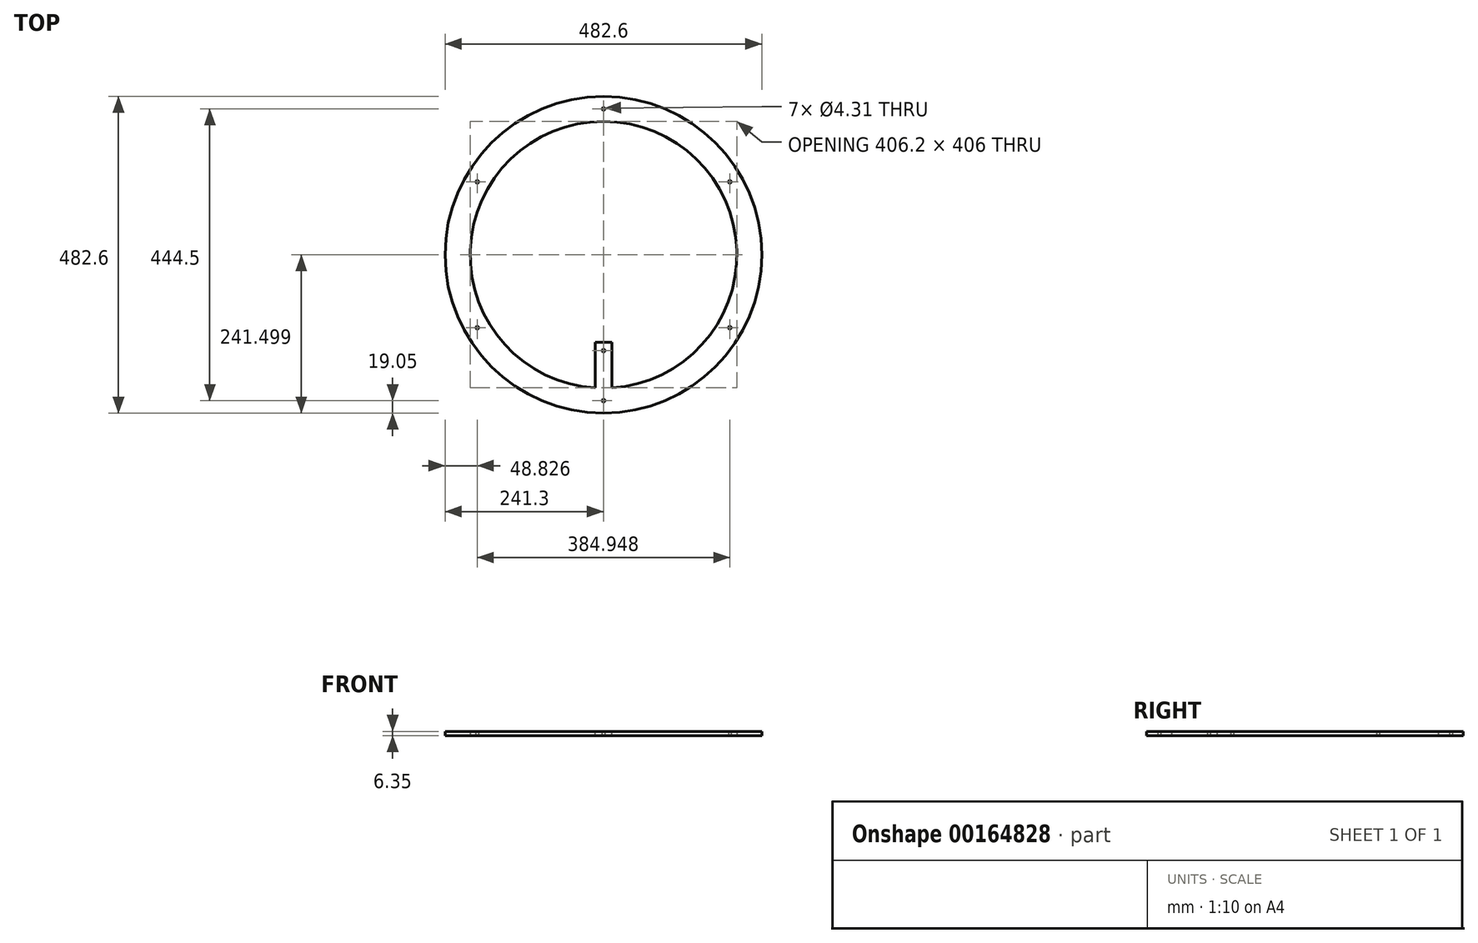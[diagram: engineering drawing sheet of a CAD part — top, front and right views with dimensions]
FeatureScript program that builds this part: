
annotation { "Feature Type Name" : "Feature", "Feature Type Description" : "" }
export const myFeature = defineFeature(function(context is Context, id is Id, definition is map)
    precondition{}
    {
        {
            var Q0;
            Q0=qCreatedBy(makeId("Top.planeOp"),FACE);
            var sketch = newSketch(context, id + "F0", { "sketchPlane" : qUnion([Q0])});
            skCircle(sketch, "E0", {"center": v(0, 0) * mm, "radius": 241.3 * mm});
            skCircle(sketch, "E1", {"center": v(0, 0) * mm, "radius": 203.2 * mm});
            skCircle(sketch, "E2.cCircle", {"center": v(0, 0) * mm, "radius": 192.47 * mm, "construction": true});
            skLineSegment(sketch, "E2.0", {"start": v(192.47, 111.13) * mm, "end": v(192.47, -111.12) * mm, "construction": true});
            skLineSegment(sketch, "E2.1", {"start": v(192.47, -111.12) * mm, "end": v(0, -222.25) * mm, "construction": true});
            skLineSegment(sketch, "E2.2", {"start": v(0, -222.25) * mm, "end": v(-192.47, -111.12) * mm, "construction": true});
            skLineSegment(sketch, "E2.3", {"start": v(-192.47, -111.13) * mm, "end": v(-192.47, 111.12) * mm, "construction": true});
            skLineSegment(sketch, "E2.4", {"start": v(-192.47, 111.12) * mm, "end": v(0, 222.25) * mm, "construction": true});
            skLineSegment(sketch, "E2.5", {"start": v(0, 222.25) * mm, "end": v(192.47, 111.12) * mm, "construction": true});
            skCircle(sketch, "E3", {"center": v(192.47, -111.12) * mm, "radius": 19.05 * mm, "construction": true});
            skCircle(sketch, "E4", {"center": v(192.47, -111.12) * mm, "radius": 2.15 * mm});
            skCircle(sketch, "E5", {"center": v(0, -222.25) * mm, "radius": 2.15 * mm});
            skCircle(sketch, "E6", {"center": v(-192.47, -111.13) * mm, "radius": 2.15 * mm});
            skCircle(sketch, "E7", {"center": v(-192.47, 111.12) * mm, "radius": 2.15 * mm});
            skCircle(sketch, "E8", {"center": v(0, 222.25) * mm, "radius": 2.15 * mm});
            skCircle(sketch, "E9", {"center": v(192.47, 111.13) * mm, "radius": 2.15 * mm});
            skSolve(sketch);
        }
        {
            var Q0;
            Q0=qSketchRegion(id+"F0",true);
            extrude(context, id + "F1", {"entities" : qUnion([Q0]), "depth" : 6.35 * mm});
        }
        {
            var Q0;
            Q0=makeQuery(id+"F1.opExtrude","CAP_FACE",FACE,{"disambiguationData":[OSD([sQuery(id+"F0.wireOp",EDGE,"E0"),sQuery(id+"F0.wireOp",EDGE,"E1"),sQuery(id+"F0.wireOp",EDGE,"E4"),sQuery(id+"F0.wireOp",EDGE,"E5"),sQuery(id+"F0.wireOp",EDGE,"E6"),sQuery(id+"F0.wireOp",EDGE,"E7"),sQuery(id+"F0.wireOp",EDGE,"E8"),sQuery(id+"F0.wireOp",EDGE,"E9")])],"isStart":false});
            var sketch = newSketch(context, id + "F2", { "sketchPlane" : qUnion([Q0])});
            skLineSegment(sketch, "E10.bottom", {"start": v(-12.7, -202.8) * mm, "end": v(12.7, -202.8) * mm});
            skLineSegment(sketch, "E10.top", {"start": v(-12.7, -133.35) * mm, "end": v(12.7, -133.35) * mm});
            skLineSegment(sketch, "E10.left", {"start": v(-12.7, -202.8) * mm, "end": v(-12.7, -133.35) * mm});
            skLineSegment(sketch, "E10.right", {"start": v(12.7, -202.8) * mm, "end": v(12.7, -133.35) * mm});
            skArc(sketch, "E11", {"start": v(-12.7, -202.8) * mm, "mid": v(0, -203.2) * mm, "end": v(12.7, -202.8) * mm});
            skLineSegment(sketch, "E12", {"start": v(0, -133.35) * mm, "end": v(0, -146.05) * mm, "construction": true});
            skLineSegment(sketch, "E13", {"start": v(0, -146.05) * mm, "end": v(12.7, -146.05) * mm, "construction": true});
            skCircle(sketch, "E14", {"center": v(0, -146.05) * mm, "radius": 2.15 * mm});
            skPoint(sketch, "E15", {"position": v(0, -222.25) * mm});
            skSolve(sketch);
        }
        {
            var Q0;
            Q0 = qSketchRegion(id + "F2", true);
            var Q1;
            Q1=makeQuery(id+"F1.opExtrude","CAP_FACE",FACE,{"disambiguationData":[OSD([sQuery(id+"F0.wireOp",EDGE,"E0"),sQuery(id+"F0.wireOp",EDGE,"E1"),sQuery(id+"F0.wireOp",EDGE,"E4"),sQuery(id+"F0.wireOp",EDGE,"E5"),sQuery(id+"F0.wireOp",EDGE,"E6"),sQuery(id+"F0.wireOp",EDGE,"E7"),sQuery(id+"F0.wireOp",EDGE,"E8"),sQuery(id+"F0.wireOp",EDGE,"E9")])],"isStart":true});
            extrude(context, id + "F3", {"entities" : qUnion([Q0]), "operationType" : NewBodyOperationType.ADD, "endBound" : BoundingType.UP_TO_SURFACE, "oppositeDirection" : true, "endBoundEntityFace" : qUnion([Q1]), "depth" : 25.4 * mm});
        }
    });
